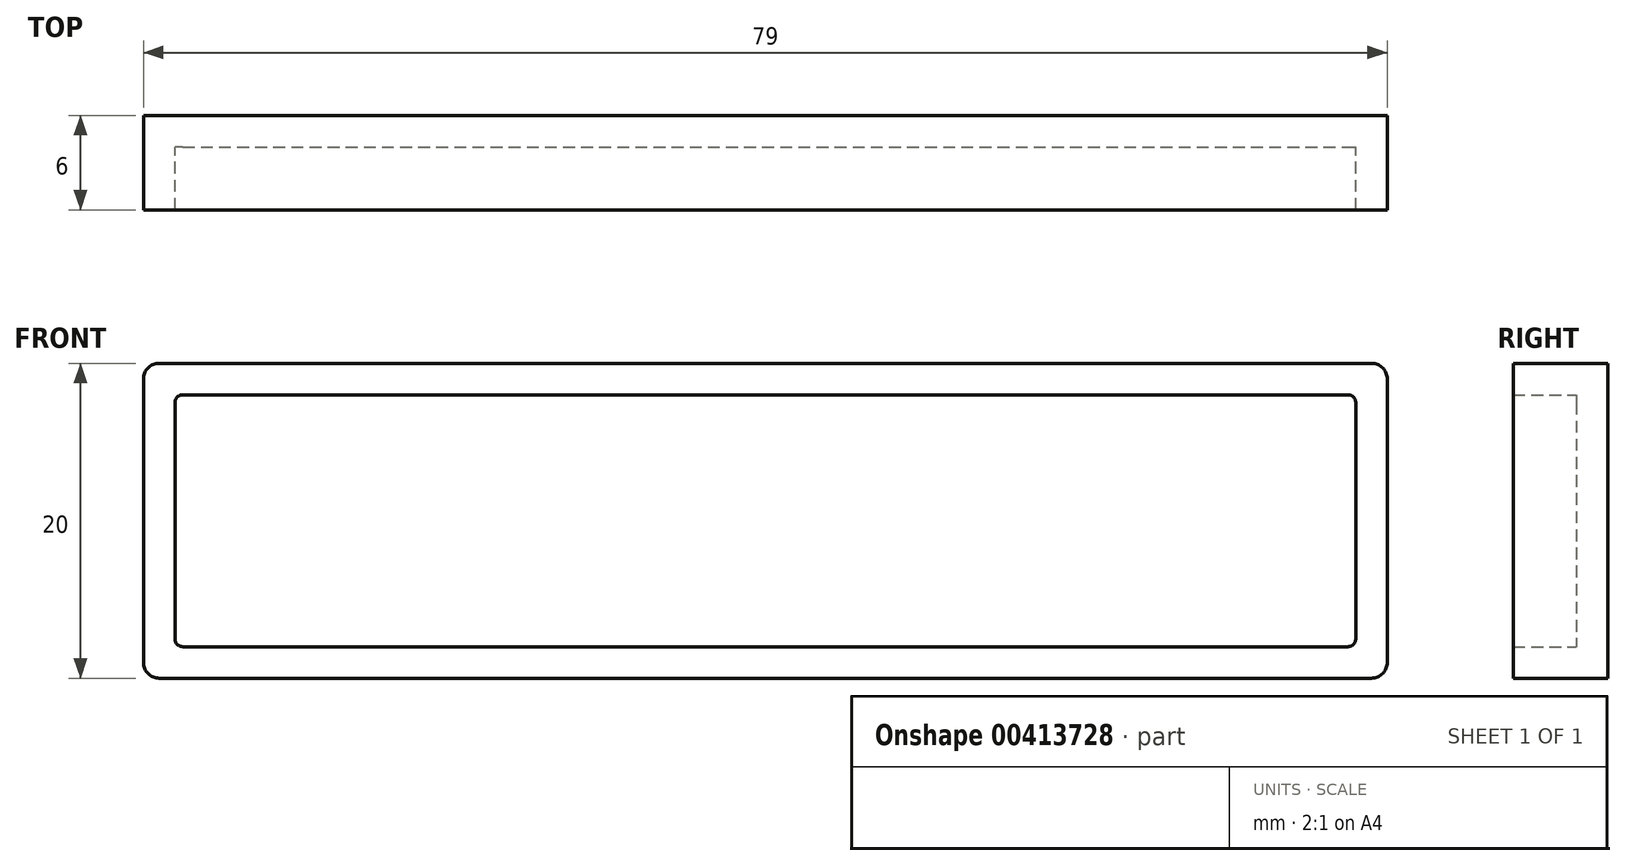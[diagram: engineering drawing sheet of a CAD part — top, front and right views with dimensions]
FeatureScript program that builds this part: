
annotation { "Feature Type Name" : "Feature", "Feature Type Description" : "" }
export const myFeature = defineFeature(function(context is Context, id is Id, definition is map)
    precondition{}
    {
        {
            var Q0;
            Q0=qCreatedBy(makeId("Front.planeOp"),FACE);
            var sketch = newSketch(context, id + "F0", { "sketchPlane" : qUnion([Q0])});
            skLineSegment(sketch, "E0.bottom", {"start": v(-39.5, 10) * mm, "end": v(39.5, 10) * mm});
            skLineSegment(sketch, "E0.top", {"start": v(-39.5, -10) * mm, "end": v(39.5, -10) * mm});
            skLineSegment(sketch, "E0.left", {"start": v(-39.5, 10) * mm, "end": v(-39.5, -10) * mm});
            skLineSegment(sketch, "E0.right", {"start": v(39.5, 10) * mm, "end": v(39.5, -10) * mm});
            skLineSegment(sketch, "E1", {"start": v(0, 16.16) * mm, "end": v(0, -15.02) * mm, "construction": true});
            skLineSegment(sketch, "E2", {"start": v(-43.95, 0) * mm, "end": v(44.07, 0) * mm, "construction": true});
            skSolve(sketch);
        }
        {
            var Q0;
            Q0 = qSketchRegion(id + "F0", true);
            extrude(context, id + "F1", {"entities" : qUnion([Q0]), "depth" : 6 * mm});
        }
        {
            var Q0;
            Q0=makeQuery(id+"F1.opExtrude","CAP_FACE",FACE,{"disambiguationData":[OSD([sQuery(id+"F0.wireOp",EDGE,"E0.bottom"),sQuery(id+"F0.wireOp",EDGE,"E0.top"),sQuery(id+"F0.wireOp",EDGE,"E0.left"),sQuery(id+"F0.wireOp",EDGE,"E0.right")])],"isStart":false});
            shell(context, id + "F2", {"entities" : qUnion([Q0]), "thickness" : 2 * mm});
        }
        {
            var Q0;
            Q0=makeQuery(id+"F1.opExtrude","SWEPT_EDGE",EDGE,{"disambiguationData":[OSD([sQuery(id+"F0.wireOp",EDGE,"E0.top"),sQuery(id+"F0.wireOp",EDGE,"E0.right")])]});
            var Q1;
            Q1=makeQuery(id+"F1.opExtrude","SWEPT_EDGE",EDGE,{"disambiguationData":[OSD([sQuery(id+"F0.wireOp",EDGE,"E0.top"),sQuery(id+"F0.wireOp",EDGE,"E0.left")])]});
            var Q2;
            Q2=makeQuery(id+"F1.opExtrude","SWEPT_EDGE",EDGE,{"disambiguationData":[OSD([sQuery(id+"F0.wireOp",EDGE,"E0.bottom"),sQuery(id+"F0.wireOp",EDGE,"E0.left")])]});
            var Q3;
            Q3=makeQuery(id+"F1.opExtrude","SWEPT_EDGE",EDGE,{"disambiguationData":[OSD([sQuery(id+"F0.wireOp",EDGE,"E0.bottom"),sQuery(id+"F0.wireOp",EDGE,"E0.right")])]});
            fillet(context, id + "F3", {"entities" : qUnion([Q0, Q1, Q2, Q3]), "radius" : 1 * mm, "tangentPropagation" : true, "allowEdgeOverflow" : false});
        }
        {
            var Q0;
            Q0=makeQuery(id+"F2.opShell","OFFSET_EDGE",EDGE,{"disambiguationData":[OSD([sQuery(id+"F0.wireOp",EDGE,"E0.top"),sQuery(id+"F0.wireOp",EDGE,"E0.left")])]});
            var Q1;
            Q1=makeQuery(id+"F2.opShell","OFFSET_EDGE",EDGE,{"disambiguationData":[OSD([sQuery(id+"F0.wireOp",EDGE,"E0.top"),sQuery(id+"F0.wireOp",EDGE,"E0.right")])]});
            var Q2;
            Q2=makeQuery(id+"F2.opShell","OFFSET_EDGE",EDGE,{"disambiguationData":[OSD([sQuery(id+"F0.wireOp",EDGE,"E0.bottom"),sQuery(id+"F0.wireOp",EDGE,"E0.right")])]});
            var Q3;
            Q3=makeQuery(id+"F2.opShell","OFFSET_EDGE",EDGE,{"disambiguationData":[OSD([sQuery(id+"F0.wireOp",EDGE,"E0.bottom"),sQuery(id+"F0.wireOp",EDGE,"E0.left")])]});
            fillet(context, id + "F4", {"entities" : qUnion([Q0, Q1, Q2, Q3]), "radius" : 0.5 * mm, "tangentPropagation" : true, "allowEdgeOverflow" : false});
        }
    });
